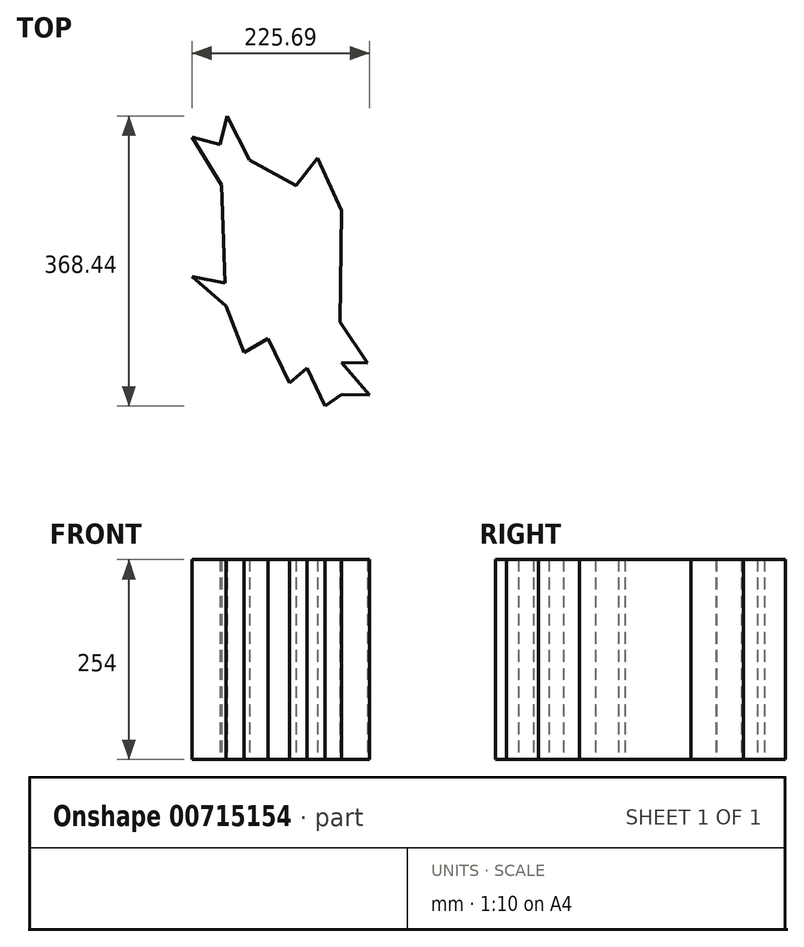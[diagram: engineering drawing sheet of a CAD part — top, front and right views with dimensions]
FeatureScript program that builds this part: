
annotation { "Feature Type Name" : "Feature", "Feature Type Description" : "" }
export const myFeature = defineFeature(function(context is Context, id is Id, definition is map)
    precondition{}
    {
        {
            var Q0;
            Q0=qCreatedBy(makeId("Top.planeOp"),FACE);
            var sketch = newSketch(context, id + "F0", { "sketchPlane" : qUnion([Q0])});
            skLineSegment(sketch, "E0", {"start": v(-146.7, -121.78) * mm, "end": v(0, -234.14) * mm});
            skLineSegment(sketch, "E1", {"start": v(-2.97, -234.14) * mm, "end": v(0, 0) * mm});
            skLineSegment(sketch, "E2", {"start": v(-1.14, -1.18) * mm, "end": v(-146.7, -121.78) * mm});
            skLineSegment(sketch, "E3", {"start": v(-146.7, -121.78) * mm, "end": v(-154.19, 83.86) * mm});
            skLineSegment(sketch, "E4", {"start": v(-154.19, 83.86) * mm, "end": v(0, 0) * mm});
            skLineSegment(sketch, "E5", {"start": v(0, 0) * mm, "end": v(54, -62.32) * mm});
            skLineSegment(sketch, "E6", {"start": v(54, -62.32) * mm, "end": v(0, -62.32) * mm});
            skLineSegment(sketch, "E7", {"start": v(0, 0) * mm, "end": v(-30.73, 66.35) * mm});
            skLineSegment(sketch, "E8", {"start": v(-30.73, 66.35) * mm, "end": v(-57.57, 31.31) * mm});
            skLineSegment(sketch, "E9", {"start": v(-57.97, 33.9) * mm, "end": v(-103.17, 104.96) * mm});
            skLineSegment(sketch, "E10", {"start": v(-103.17, 104.96) * mm, "end": v(-116.96, 63.62) * mm});
            skLineSegment(sketch, "E11", {"start": v(-116.96, 63.62) * mm, "end": v(-146.7, 122.96) * mm});
            skLineSegment(sketch, "E12", {"start": v(-144.37, 122.96) * mm, "end": v(-154.19, 83.86) * mm});
            skLineSegment(sketch, "E13", {"start": v(-154.19, 83.86) * mm, "end": v(-190.1, 92.88) * mm});
            skLineSegment(sketch, "E14", {"start": v(-190.1, 92.88) * mm, "end": v(-152.3, 32.02) * mm});
            skLineSegment(sketch, "E15", {"start": v(-155.53, 31.9) * mm, "end": v(-190.1, 32.34) * mm});
            skLineSegment(sketch, "E16", {"start": v(-188.4, 32.77) * mm, "end": v(-149.87, -34.83) * mm});
            skLineSegment(sketch, "E17", {"start": v(-149.87, -34.83) * mm, "end": v(-190.1, -34.32) * mm});
            skLineSegment(sketch, "E18", {"start": v(-190.1, -42.3) * mm, "end": v(-146.7, -92.38) * mm});
            skLineSegment(sketch, "E19", {"start": v(-146.7, -92.38) * mm, "end": v(-190.1, -84.26) * mm});
            skLineSegment(sketch, "E20", {"start": v(-190.1, -84.26) * mm, "end": v(-146.7, -121.78) * mm});
            skLineSegment(sketch, "E21", {"start": v(-146.7, -121.78) * mm, "end": v(-124.11, -180.82) * mm});
            skLineSegment(sketch, "E22", {"start": v(-124.11, -180.82) * mm, "end": v(-93.5, -162.53) * mm});
            skLineSegment(sketch, "E23", {"start": v(-93.5, -162.53) * mm, "end": v(-65.87, -219.27) * mm});
            skLineSegment(sketch, "E24", {"start": v(-65.87, -219.27) * mm, "end": v(-44.08, -200.38) * mm});
            skLineSegment(sketch, "E25", {"start": v(-44.08, -200.38) * mm, "end": v(-20.75, -248.58) * mm});
            skLineSegment(sketch, "E26", {"start": v(-20.75, -248.58) * mm, "end": v(0, -234.14) * mm});
            skLineSegment(sketch, "E27", {"start": v(0, -234.14) * mm, "end": v(35.58, -234.6) * mm});
            skLineSegment(sketch, "E28", {"start": v(35.58, -234.6) * mm, "end": v(0, -193.53) * mm});
            skLineSegment(sketch, "E29", {"start": v(0, -193.53) * mm, "end": v(35.58, -193.98) * mm});
            skLineSegment(sketch, "E30", {"start": v(34.9, -196.6) * mm, "end": v(-1.8, -141.76) * mm});
            skLineSegment(sketch, "E31", {"start": v(-1.8, -141.76) * mm, "end": v(35.58, -142.24) * mm});
            skLineSegment(sketch, "E32", {"start": v(36.88, -148.46) * mm, "end": v(0, -92.38) * mm});
            skLineSegment(sketch, "E33", {"start": v(-0.42, -87.47) * mm, "end": v(35.58, -103.34) * mm});
            skLineSegment(sketch, "E34", {"start": v(39.03, -103.34) * mm, "end": v(4.66, -62.32) * mm});
            skSolve(sketch);
        }
        {
            var Q0;
            Q0 = qSketchRegion(id + "F0", true);
            extrude(context, id + "F1", {"entities" : qUnion([Q0]), "depth" : 254 * mm, "offsetDistance" : 25.4 * mm});
        }
    });
